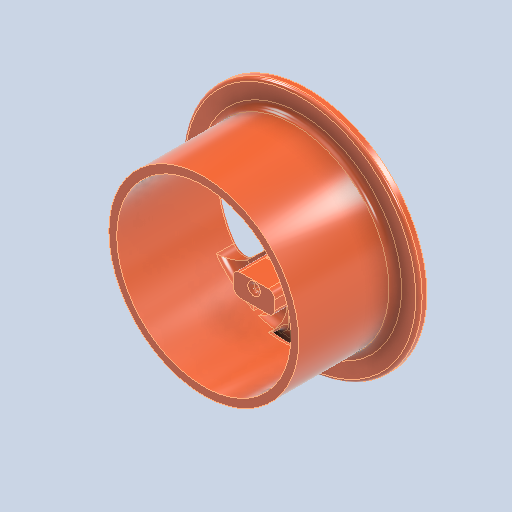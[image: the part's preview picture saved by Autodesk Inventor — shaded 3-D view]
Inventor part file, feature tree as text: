
AUTODESK INVENTOR PART (.ipt)
format: ipt  version: 2023.2 (Build 272271000, 271)  size: 686,592 bytes
history: native  units: mm
features: fillet x9, sketch x6, extrude x5, hole x1
ambient origin geometry x8: Origin, YZ Plane, XZ Plane, XY Plane, X Axis, Y Axis, Z Axis, Center Point
bodies: Solid1 (feature_tree)
feature tree (21):
  extrude  "Extrusion1"  Depth=2.5mm
  extrude  "Extrusion2"  Depth=2.5mm TaperAngle=0.0deg
  extrude  "Extrusion3"  Depth=10.0mm
  hole  "Hole1"  [1 undecoded]
  extrude  "Extrusion5"  Depth=55.0mm
  fillet  "Fillet1"  Radius=17.1mm
  extrude  "Extrusion6"  Depth=1.0mm
  fillet  "Fillet2"  Radius=5.0mm
  fillet  "Fillet3"  Radius=5.0mm
  fillet  "Fillet4"  Radius=25.1mm
  fillet  "Fillet5"  Radius=2.0mm
  fillet  "Fillet7"  Radius=2.0mm
  fillet  "Fillet8"  Radius=5.0mm
  fillet  "Fillet9"  Radius=8.5mm
  fillet  "Fillet10"  Radius=10.0mm
  sketch  "Sketch1"  dims[d0=60.0mm d1=2.5mm]
  sketch  "Sketch2"  dims[d2=33.0mm d3=0.0mm d5=2.5mm d6=0.0mm]
  sketch  "Sketch3"  dims[d7=55.0mm d8=10.0mm]
  sketch  "Sketch4"  dims[d9=16.8mm d10=6.4mm]
  sketch  "Sketch6"  dims[d11=13.0mm d12=55.0mm d14=16.8mm d15=6.4mm d16=13.0mm d17=17.1mm d18=0.0mm]
  sketch  "Sketch7"  dims[d19=27.8mm d20=8.7mm d21=2.0mm d22=6.0mm d23=4.0mm d24=2.0mm d25=90.0deg d26=7.0mm d27=0.0mm d32=5.0mm d33=5.0mm d34=25.1mm d35=0.0mm d36=2.0mm d37=2.0mm d38=5.0mm d39=8.5mm d40=10.0mm d41=0.0mm d42=4.0mm d43=2.0mm d44=2.0mm d45=2.0mm d47=1.0mm d48=1.0mm d49=2.0mm d50=1.0mm]
note: 1 required parameter value undecoded (feature->parameter linkage not recoverable at this tier; creation-order binding heuristic only, values carry confidence <= 0.55)
